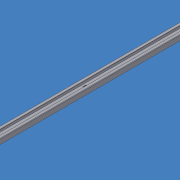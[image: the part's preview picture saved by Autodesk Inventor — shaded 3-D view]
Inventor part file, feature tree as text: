
AUTODESK INVENTOR PART (.ipt)
format: ipt  version: 2015 (Build 190159000, 159)  size: 273,408 bytes
history: native  units: mm
features: sheet_metal_op x9, other x8, sketch x6, plane x2
ambient origin geometry x8: Origin, YZ Plane, XZ Plane, XY Plane, X Axis, Y Axis, Z Axis, Center Point
bodies: Solid1 (feature_tree)
feature tree (25):
  sheet_metal_op  "Face1"
  sheet_metal_op  "Flange1"
  sheet_metal_op  "Flange2"
  sheet_metal_op  "Flange3"
  sheet_metal_op  "Flange4"
  plane  "Work Plane4"
  plane  "Work Plane6"
  sketch  "Sketch1"  dims[d4=0.001mm]
  other  "Plate1"
  sketch  "Sketch2"  dims[d5=3.0mm]
  other  "Plate2"
  sheet_metal_op  "Bend1"
  sketch  "Sketch3"  dims[d6=0.001mm]
  other  "Plate3"
  sheet_metal_op  "Bend2"
  sketch  "Sketch4"  dims[d7=6.0mm]
  other  "Plate4"
  sheet_metal_op  "Bend3"
  sketch  "Sketch5"  dims[d8=0.001mm]
  other  "Plate5"
  sheet_metal_op  "Bend4"
  sketch  "Sketch6"  dims[d9=29.0mm d10=90.0deg d11=0.001mm d12=3.0mm d13=0.001mm d14=6.0mm d15=0.001mm d16=29.0mm d17=90.0deg d18=0.001mm d19=3.0mm d20=0.001mm d21=6.0mm d22=0.001mm d23=15.0mm d24=90.0deg d25=0.001mm d26=3.0mm d27=0.001mm d28=6.0mm d29=0.001mm d30=15.0mm d31=90.0deg d32=0.001mm d33=4.0mm d34=20.5mm d35=4.0mm d36=20.5mm d37=0.0mm d38=33.0mm d40=4.0mm d41=0.0mm d42=1550.0mm d45=150.0mm d46=10.0mm d47=10.0mm d48=64.0mm d49=6.0mm d50=64.0mm d51=4.0mm d52=9.0mm d62=20.5mm d63=4.0mm d64=9.0mm d65=20.5mm d66=4.0mm d68=4.0mm d69=0.0mm d71=50.0mm d72=33.0mm d73=16.5mm d74=9.0mm d75=4.0mm d76=20.5mm d77=4.0mm d78=33.0mm d0=3.0mm]
  other  "FlatPattern"
  other  "Cut1"
  other  "FlatPatternExtrusion2"
